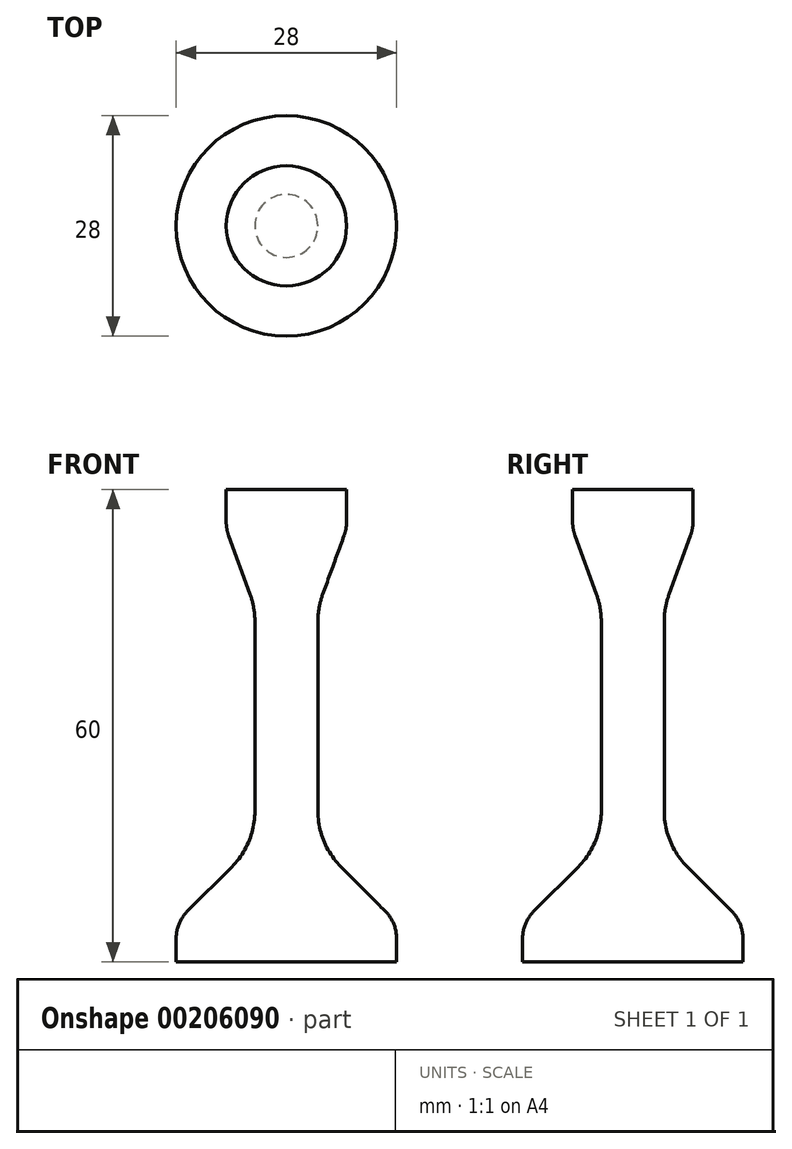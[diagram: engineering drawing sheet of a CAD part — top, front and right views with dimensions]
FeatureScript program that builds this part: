
annotation { "Feature Type Name" : "Feature", "Feature Type Description" : "" }
export const myFeature = defineFeature(function(context is Context, id is Id, definition is map)
    precondition{}
    {
        {
            var Q0;
            Q0=qCreatedBy(makeId("Front.planeOp"),FACE);
            var sketch = newSketch(context, id + "F0", { "sketchPlane" : qUnion([Q0])});
            skLineSegment(sketch, "E0", {"start": v(0, 30) * mm, "end": v(0, -30) * mm});
            skLineSegment(sketch, "E1", {"start": v(0, -30) * mm, "end": v(7.64, -30) * mm});
            skLineSegment(sketch, "E2", {"start": v(7.64, -30) * mm, "end": v(7.64, -25) * mm, "construction": true});
            skLineSegment(sketch, "E3", {"start": v(7.64, -25) * mm, "end": v(4, -15) * mm, "construction": true});
            skLineSegment(sketch, "E4", {"start": v(4, -15) * mm, "end": v(4, 0) * mm});
            skLineSegment(sketch, "E5", {"start": v(4, 0) * mm, "end": v(4, 15) * mm});
            skLineSegment(sketch, "E6", {"start": v(4, 15) * mm, "end": v(7.64, 25) * mm});
            skLineSegment(sketch, "E7", {"start": v(7.64, 25) * mm, "end": v(7.64, 30) * mm});
            skLineSegment(sketch, "E8", {"start": v(7.64, 30) * mm, "end": v(0, 30) * mm});
            skLineSegment(sketch, "E9", {"start": v(4, -15) * mm, "end": v(14, -25) * mm});
            skLineSegment(sketch, "E10", {"start": v(14, -25) * mm, "end": v(14, -30) * mm});
            skLineSegment(sketch, "E11", {"start": v(14, -30) * mm, "end": v(7.64, -30) * mm});
            skSolve(sketch);
        }
        {
            var Q0;
            Q0=qSketchRegion(id+"F0",true);
            var Q1;
            Q1=sQuery(id+"F0.wireOp",EDGE,"E0");
            revolve(context, id + "F1", {"entities" : qUnion([Q0]), "axis" : qUnion([Q1]), "revolveType" : RevolveType.FULL});
        }
        {
            var Q0;
            Q0=makeQuery(id+"F1.opRevolve","SWEPT_EDGE",EDGE,{"disambiguationData":[OSD([sQuery(id+"F0.wireOp",EDGE,"E5"),sQuery(id+"F0.wireOp",EDGE,"E6")])]});
            var Q1;
            Q1=makeQuery(id+"F1.opRevolve","SWEPT_EDGE",EDGE,{"disambiguationData":[OSD([sQuery(id+"F0.wireOp",EDGE,"E3"),sQuery(id+"F0.wireOp",EDGE,"E4")])]});
            fillet(context, id + "F2", {"entities" : qUnion([Q0, Q1]), "radius" : 10 * mm, "tangentPropagation" : true, "allowEdgeOverflow" : false});
        }
        {
            var Q0;
            Q0=makeQuery(id+"F1.opRevolve","SWEPT_EDGE",EDGE,{"disambiguationData":[OSD([sQuery(id+"F0.wireOp",EDGE,"E6"),sQuery(id+"F0.wireOp",EDGE,"E7")])]});
            var Q1;
            Q1=makeQuery(id+"F1.opRevolve","SWEPT_EDGE",EDGE,{"disambiguationData":[OSD([sQuery(id+"F0.wireOp",EDGE,"E2"),sQuery(id+"F0.wireOp",EDGE,"E3")])]});
            var Q2;
            Q2=makeQuery(id+"F1.opRevolve","SWEPT_EDGE",EDGE,{"disambiguationData":[OSD([sQuery(id+"F0.wireOp",EDGE,"E9"),sQuery(id+"F0.wireOp",EDGE,"E10")])]});
            fillet(context, id + "F3", {"entities" : qUnion([Q0, Q1, Q2]), "radius" : 5 * mm, "tangentPropagation" : true, "allowEdgeOverflow" : false});
        }
    });
